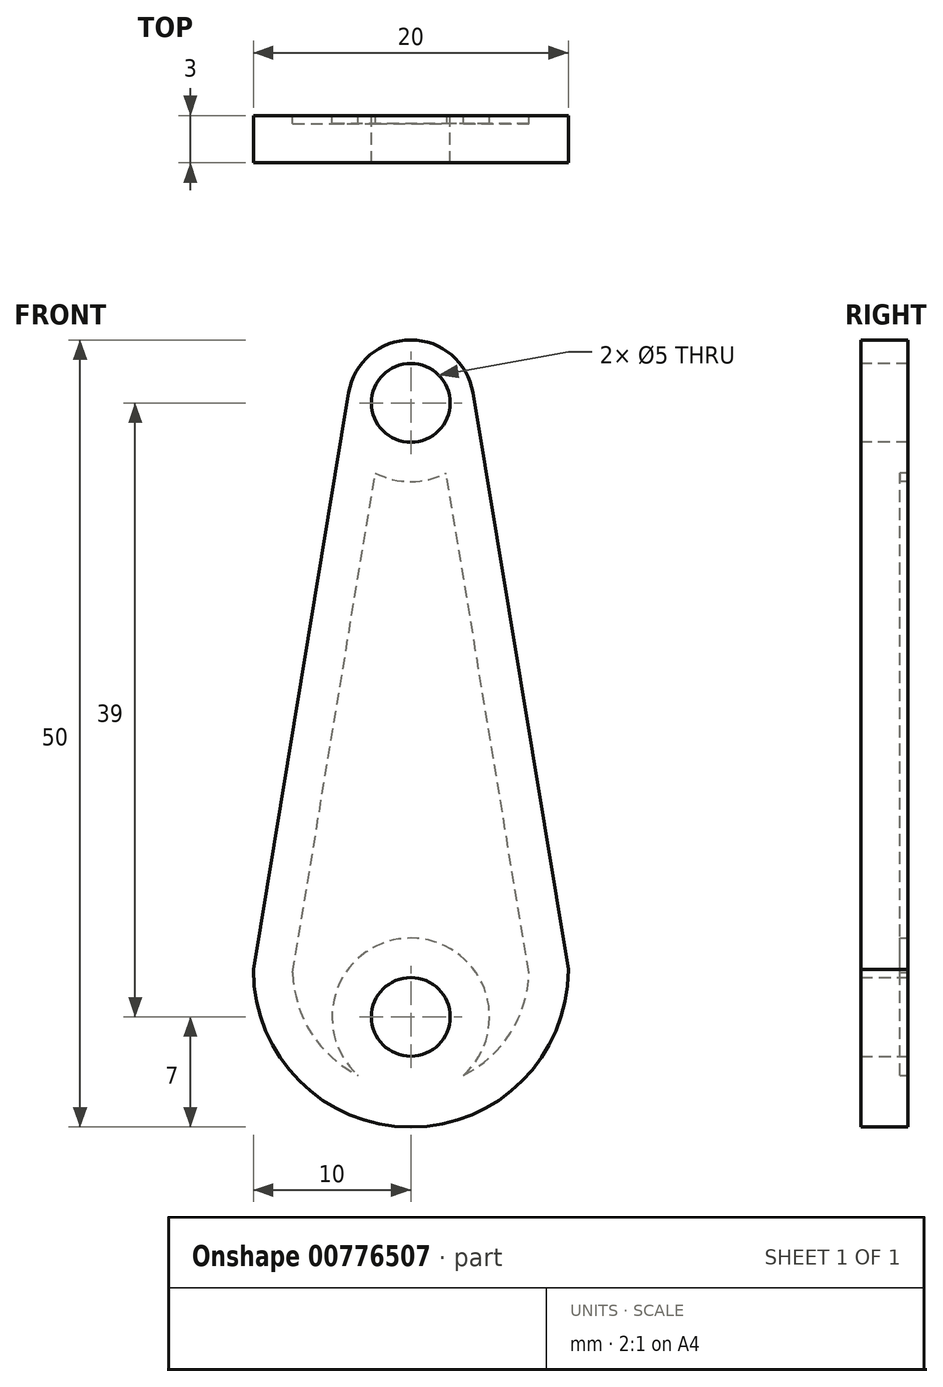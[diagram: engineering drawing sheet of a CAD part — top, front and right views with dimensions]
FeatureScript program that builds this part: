
annotation { "Feature Type Name" : "Feature", "Feature Type Description" : "" }
export const myFeature = defineFeature(function(context is Context, id is Id, definition is map)
    precondition{}
    {
        {
            var Q0;
            Q0=qCreatedBy(makeId("Front.planeOp"),FACE);
            var sketch = newSketch(context, id + "F0", { "sketchPlane" : qUnion([Q0])});
            skLineSegment(sketch, "E0.bottom", {"start": v(-10, 43) * mm, "end": v(10, 43) * mm});
            skLineSegment(sketch, "E0.top", {"start": v(-10, -7) * mm, "end": v(10, -7) * mm});
            skLineSegment(sketch, "E0.left", {"start": v(-10, 43) * mm, "end": v(-10, -7) * mm});
            skLineSegment(sketch, "E0.right", {"start": v(10, 43) * mm, "end": v(10, -7) * mm});
            skCircle(sketch, "E1", {"center": v(0, 0) * mm, "radius": 2.5 * mm});
            skSolve(sketch);
        }
        {
            var Q0;
            Q0=makeQuery(id+"F0.imprint","IMPRINT",FACE,{"disambiguationData":[TD([[makeQuery(id+"F0.imprint","IMPRINT",EDGE,{"derivedFrom":sQuery(id+"F0.wireOp",EDGE,"E0.bottom")}),-1.0]])]});
            extrude(context, id + "F1", {"entities" : qUnion([Q0]), "depth" : 3 * mm, "offsetDistance" : 25 * mm});
        }
        {
            var Q0;
            Q0=makeQuery(id+"F1.opExtrude","SWEPT_EDGE",EDGE,{"disambiguationData":[OSD([sQuery(id+"F0.wireOp",EDGE,"E0.top"),sQuery(id+"F0.wireOp",EDGE,"E0.left")])]});
            var Q1;
            Q1=makeQuery(id+"F1.opExtrude","SWEPT_EDGE",EDGE,{"disambiguationData":[OSD([sQuery(id+"F0.wireOp",EDGE,"E0.top"),sQuery(id+"F0.wireOp",EDGE,"E0.right")])]});
            fillet(context, id + "F2", {"entities" : qUnion([Q0, Q1]), "radius" : 10 * mm, "tangentPropagation" : true, "allowEdgeOverflow" : false});
        }
        {
            var Q0;
            Q0=makeQuery(id+"F1.opExtrude","CAP_FACE",FACE,{"disambiguationData":[OSD([sQuery(id+"F0.wireOp",EDGE,"E0.bottom"),sQuery(id+"F0.wireOp",EDGE,"E0.top"),sQuery(id+"F0.wireOp",EDGE,"E0.left"),sQuery(id+"F0.wireOp",EDGE,"E0.right"),sQuery(id+"F0.wireOp",EDGE,"E1")])],"isStart":false});
            var sketch = newSketch(context, id + "F3", { "sketchPlane" : qUnion([Q0])});
            skArc(sketch, "E2", {"start": v(3.95, 39.65) * mm, "mid": v(0, 43) * mm, "end": v(-3.95, 39.65) * mm});
            skLineSegment(sketch, "E3", {"start": v(-10, 3) * mm, "end": v(-3.95, 39.65) * mm});
            skLineSegment(sketch, "E4", {"start": v(10, 3) * mm, "end": v(3.95, 39.65) * mm});
            skSolve(sketch);
        }
        {
            var Q0;
            {var subQ0=sQuery(id+"F3.wireOp",EDGE,"E4");Q0=makeQuery(id+"F3.imprint","IMPRINT",FACE,{"disambiguationData":[TD([[makeQuery(id+"F3.imprint","IMPRINT",EDGE,{"derivedFrom":subQ0}),-1.0]])]});}
            var Q1;
            {var subQ0=sQuery(id+"F3.wireOp",EDGE,"E3");Q1=makeQuery(id+"F3.imprint","IMPRINT",FACE,{"disambiguationData":[TD([[makeQuery(id+"F3.imprint","IMPRINT",EDGE,{"derivedFrom":subQ0}),1.0]])]});}
            extrude(context, id + "F4", {"entities" : qUnion([Q0, Q1]), "operationType" : NewBodyOperationType.REMOVE, "endBound" : BoundingType.THROUGH_ALL, "oppositeDirection" : true, "depth" : 25 * mm, "offsetDistance" : 25 * mm});
        }
        {
            var Q0;
            Q0=makeQuery(id+"F1.opExtrude","CAP_FACE",FACE,{"disambiguationData":[OSD([sQuery(id+"F0.wireOp",EDGE,"E0.bottom"),sQuery(id+"F0.wireOp",EDGE,"E0.top"),sQuery(id+"F0.wireOp",EDGE,"E0.left"),sQuery(id+"F0.wireOp",EDGE,"E0.right"),sQuery(id+"F0.wireOp",EDGE,"E1")])],"isStart":false});
            var sketch = newSketch(context, id + "F5", { "sketchPlane" : qUnion([Q0])});
            skCircle(sketch, "E5", {"center": v(0, 39) * mm, "radius": 2.5 * mm});
            skSolve(sketch);
        }
        {
            var Q0;
            Q0=makeQuery(id+"F5.imprint","IMPRINT",FACE,{"disambiguationData":[TD([[makeQuery(id+"F5.imprint","IMPRINT",EDGE,{"derivedFrom":sQuery(id+"F5.wireOp",EDGE,"E5")}),1.0]])]});
            extrude(context, id + "F6", {"entities" : qUnion([Q0]), "operationType" : NewBodyOperationType.REMOVE, "endBound" : BoundingType.THROUGH_ALL, "oppositeDirection" : true, "depth" : 25 * mm, "offsetDistance" : 25 * mm});
        }
        {
            var Q0;
            Q0=makeQuery(id+"F1.opExtrude","CAP_FACE",FACE,{"disambiguationData":[OSD([sQuery(id+"F0.wireOp",EDGE,"E0.bottom"),sQuery(id+"F0.wireOp",EDGE,"E0.top"),sQuery(id+"F0.wireOp",EDGE,"E0.left"),sQuery(id+"F0.wireOp",EDGE,"E0.right"),sQuery(id+"F0.wireOp",EDGE,"E1")])],"isStart":true});
            shell(context, id + "F7", {"entities" : qUnion([Q0]), "thickness" : 2.5 * mm});
        }
    });
